# Revit family: Cabinet-Teknion-CETO_Tall_Cabinet_Open-R2023
name_source: partatom
category: Furniture
units: mm (PartAtom-declared; Revit-internal decimal feet)

## family parameters
Always vertical = Yes
Cut with Voids When Loaded = No
Enable Cutting in Views = No
OmniClass Number = 23.40.20.00
OmniClass Title = General Furniture and Specialties
Render Appearance Source = Family Geometry
Room Calculation Point = No
Shared = Yes
Work Plane-Based = No

## types (4) — shared parameters
Actual Depth = 25.024 "
Assembly Code = E2020200
Manufacturer = Teknion
Manufacturer Fax = 416.661.4586
Part Number = CETO
Product Documentation Link = https://www.teknion.com
Product Line = Storage Cabinets
Product Page URL = https://www.teknion.com
Series = Expansion Casework+
Sustainability Data = https://www.teknion.com
URL = www.teknion.com
Unit Weight URL = http://www.teknion.com
Warranty = http://www.teknion.com
zero-valued in all types: Default Elevation

## per-type parameters (varying)
| type | Description | Fixed Shelf | Fixed Shelf Dim | Height | Lower Shelf Dim | Model |
| 24D,72H | Tall Cabinet – Open, 24D, 72H | No | 31.325 " | 72 " | 31.35 " | CETO24__72 |
| 24D,84H | Tall Cabinet – Open, 24D, 84H | No | 36 " | 84 " | 36.299 " | CETO24__84 |
| 24D,90H | Tall Cabinet – Open, 24D, 90H | Yes | 29.709 " | 90 " | 36.299 " | CETO24__90 |
| 24D,96H | Tall Cabinet – Open, 24D, 96H | Yes | 35.709 " | 96 " | 36.299 " | CETO24__96 |

## geometry (parser evidence)
native form markers: Sweep x3
no freeform markers — native parametric forms only
